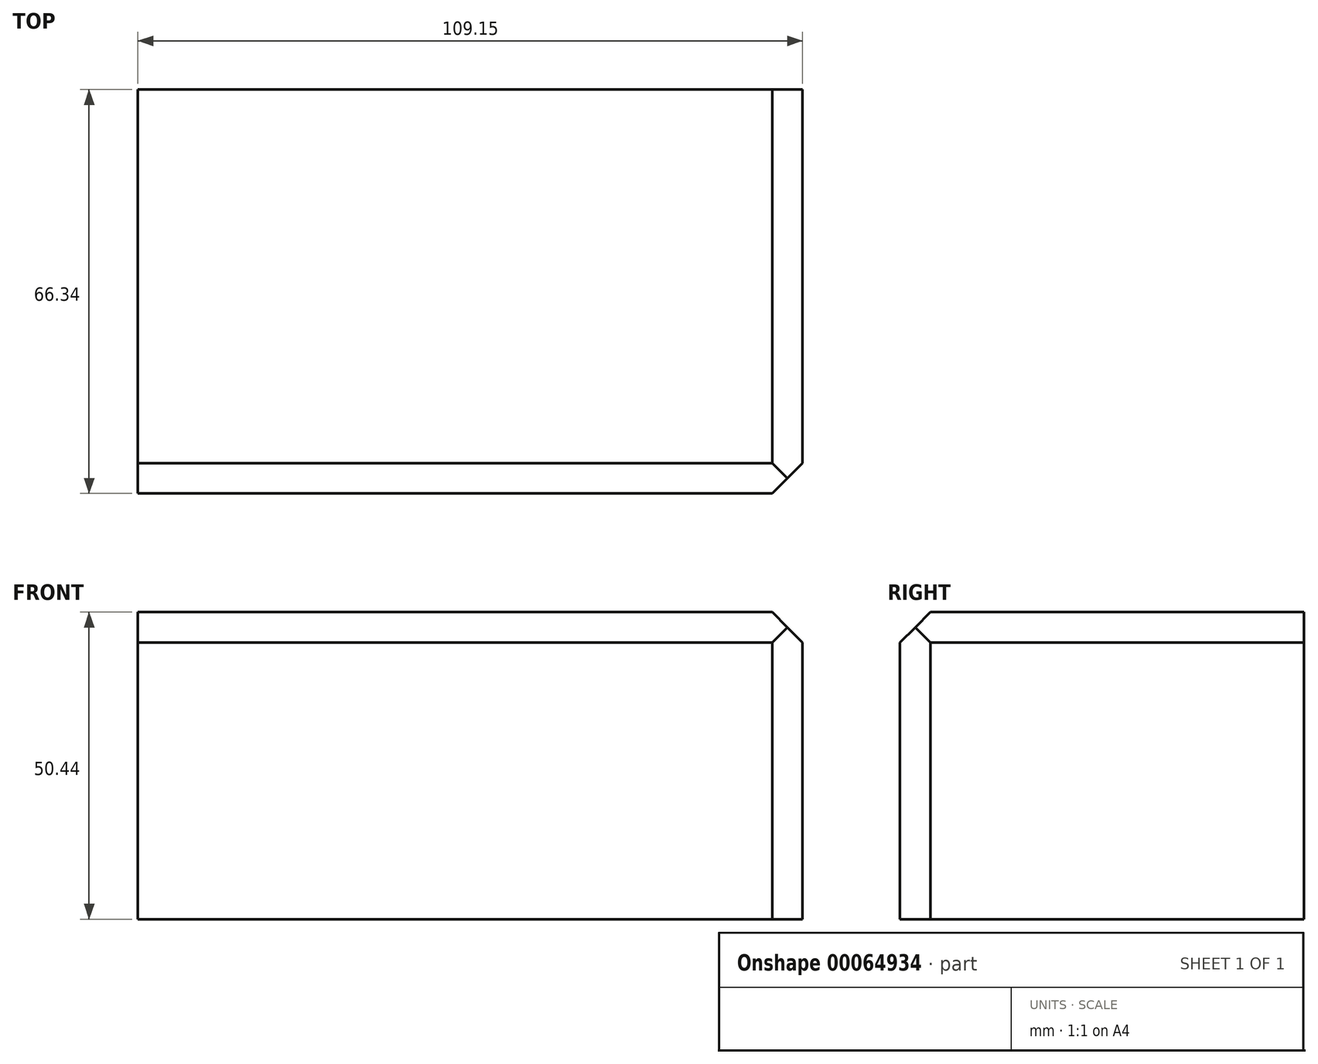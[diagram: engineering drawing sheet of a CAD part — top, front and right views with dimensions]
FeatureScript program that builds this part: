
annotation { "Feature Type Name" : "Feature", "Feature Type Description" : "" }
export const myFeature = defineFeature(function(context is Context, id is Id, definition is map)
    precondition{}
    {
        {
            var Q0;
            Q0=qCreatedBy(makeId("Front.planeOp"),FACE);
            var sketch = newSketch(context, id + "F0", { "sketchPlane" : qUnion([Q0])});
            skLineSegment(sketch, "E0.bottom", {"start": v(0, 0) * mm, "end": v(-109.15, 0) * mm});
            skLineSegment(sketch, "E0.top", {"start": v(0, 50.44) * mm, "end": v(-109.15, 50.44) * mm});
            skLineSegment(sketch, "E0.left", {"start": v(0, 0) * mm, "end": v(0, 50.44) * mm});
            skLineSegment(sketch, "E0.right", {"start": v(-109.15, 0) * mm, "end": v(-109.15, 50.44) * mm});
            skSolve(sketch);
        }
        {
            var Q0;
            Q0 = qSketchRegion(id + "F0", true);
            extrude(context, id + "F1", {"entities" : qUnion([Q0]), "depth" : 66.34 * mm});
        }
        {
            var Q0;
            Q0=makeQuery(id+"F1.opExtrude","SWEPT_EDGE",EDGE,{"disambiguationData":[OSD([sQuery(id+"F0.wireOp",EDGE,"E0.top"),sQuery(id+"F0.wireOp",EDGE,"E0.left")])]});
            var Q1;
            Q1=makeQuery(id+"F1.opExtrude","CAP_EDGE",EDGE,{"disambiguationData":[OSD([sQuery(id+"F0.wireOp",EDGE,"E0.left")])],"isStart":false});
            chamfer(context, id + "F2", {"entities" : qUnion([Q0, Q1]), "width" : 5 * mm, "tangentPropagation" : true});
        }
        {
            var Q0;
            Q0=makeQuery(id+"F1.opExtrude","CAP_EDGE",EDGE,{"disambiguationData":[OSD([sQuery(id+"F0.wireOp",EDGE,"E0.top")])],"isStart":false});
            chamfer(context, id + "F3", {"entities" : qUnion([Q0]), "width" : 5 * mm, "tangentPropagation" : true});
        }
    });
